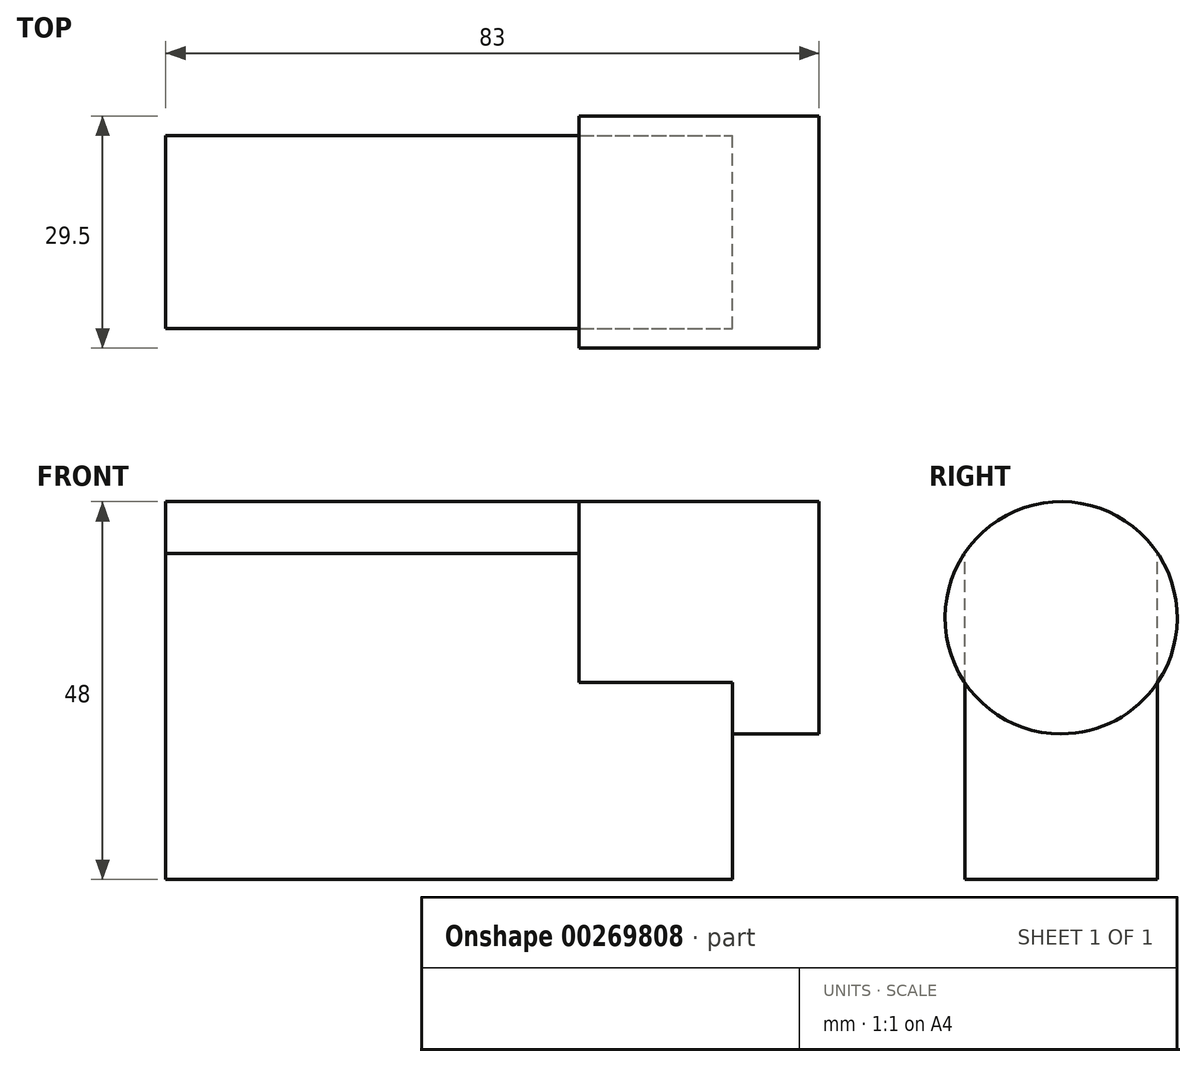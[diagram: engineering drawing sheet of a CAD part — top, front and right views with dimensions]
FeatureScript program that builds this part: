
annotation { "Feature Type Name" : "Feature", "Feature Type Description" : "" }
export const myFeature = defineFeature(function(context is Context, id is Id, definition is map)
    precondition{}
    {
        {
            var Q0;
            Q0=qCreatedBy(makeId("Top.planeOp"),FACE);
            var sketch = newSketch(context, id + "F0", { "sketchPlane" : qUnion([Q0])});
            skLineSegment(sketch, "E0.bottom", {"start": v(0, 0) * mm, "end": v(72, 0) * mm});
            skLineSegment(sketch, "E0.top", {"start": v(0, 24.5) * mm, "end": v(72, 24.5) * mm});
            skLineSegment(sketch, "E0.left", {"start": v(0, 0) * mm, "end": v(0, 24.5) * mm});
            skLineSegment(sketch, "E0.right", {"start": v(72, 0) * mm, "end": v(72, 24.5) * mm});
            skSolve(sketch);
        }
        {
            var Q0;
            Q0=makeQuery(id+"F0.imprint","IMPRINT",FACE,{"disambiguationData":[TD([[makeQuery(id+"F0.imprint","IMPRINT",EDGE,{"derivedFrom":sQuery(id+"F0.wireOp",EDGE,"E0.bottom")}),1.0]])]});
            extrude(context, id + "F1", {"entities" : qUnion([Q0]), "depth" : 18.5 * mm});
        }
        {
            var Q0;
            Q0=makeQuery(id+"F1.opExtrude","SWEPT_FACE",FACE,{"disambiguationData":[OSD([sQuery(id+"F0.wireOp",EDGE,"E0.right")])]});
            var sketch = newSketch(context, id + "F2", { "sketchPlane" : qUnion([Q0])});
            skCircle(sketch, "E1", {"center": v(12.25, 33.25) * mm, "radius": 14.75 * mm});
            skPoint(sketch, "E2", {"position": v(12.25, 18.5) * mm});
            skLineSegment(sketch, "E3", {"start": v(24.5, 18.5) * mm, "end": v(24.5, 41.44) * mm, "construction": true});
            skLineSegment(sketch, "E4", {"start": v(24.5, 41.44) * mm, "end": v(0, 41.44) * mm, "construction": true});
            skLineSegment(sketch, "E5", {"start": v(0, 41.44) * mm, "end": v(0, 18.5) * mm, "construction": true});
            skSolve(sketch);
        }
        {
            var Q0;
            Q0=makeQuery(id+"F2.imprint","IMPRINT",FACE,{"disambiguationData":[TD([[makeQuery(id+"F2.imprint","IMPRINT",EDGE,{"derivedFrom":sQuery(id+"F2.wireOp",EDGE,"E1")}),1.0]])]});
            extrude(context, id + "F3", {"entities" : qUnion([Q0]), "operationType" : NewBodyOperationType.ADD, "depth" : 11 * mm});
        }
        {
            var Q0;
            Q0=makeQuery(id+"F3.opExtrude","CAP_FACE",FACE,{"disambiguationData":[OSD([sQuery(id+"F2.wireOp",EDGE,"E1")])],"isStart":true});
            extrude(context, id + "F4", {"entities" : qUnion([Q0]), "depth" : 19.5 * mm});
        }
        {
            var Q0;
            Q0=makeQuery(id+"F1.opExtrude","CAP_FACE",FACE,{"disambiguationData":[OSD([sQuery(id+"F0.wireOp",EDGE,"E0.bottom"),sQuery(id+"F0.wireOp",EDGE,"E0.top"),sQuery(id+"F0.wireOp",EDGE,"E0.left"),sQuery(id+"F0.wireOp",EDGE,"E0.right")])],"isStart":false});
            var sketch = newSketch(context, id + "F5", { "sketchPlane" : qUnion([Q0])});
            skLineSegment(sketch, "E6.bottom", {"start": v(0, 0) * mm, "end": v(72, 0) * mm});
            skLineSegment(sketch, "E6.top", {"start": v(0, 24.5) * mm, "end": v(72, 24.5) * mm});
            skLineSegment(sketch, "E6.left", {"start": v(0, 0) * mm, "end": v(0, 24.5) * mm});
            skLineSegment(sketch, "E6.right", {"start": v(72, 0) * mm, "end": v(72, 24.5) * mm});
            skSolve(sketch);
        }
        {
            var Q0;
            Q0 = qSketchRegion(id + "F5", true);
            extrude(context, id + "F6", {"entities" : qUnion([Q0]), "operationType" : NewBodyOperationType.ADD, "depth" : 22.95 * mm});
        }
        {
            var Q0;
            Q0=makeQuery(id+"F6.opExtrude","SWEPT_FACE",FACE,{"disambiguationData":[OSD([sQuery(id+"F5.wireOp",EDGE,"E6.left")])]});
            var sketch = newSketch(context, id + "F7", { "sketchPlane" : qUnion([Q0])});
            skArc(sketch, "E7", {"start": v(0, 41.44) * mm, "mid": v(-12.25, 48) * mm, "end": v(-24.5, 41.44) * mm});
            skSolve(sketch);
        }
        {
            var Q0;
            Q0=makeQuery(id+"F7.imprint","IMPRINT",FACE,{"disambiguationData":[TD([[makeQuery(id+"F7.imprint","IMPRINT",EDGE,{"derivedFrom":sQuery(id+"F7.wireOp",EDGE,"E7")}),1.0]])]});
            extrude(context, id + "F8", {"entities" : qUnion([Q0]), "operationType" : NewBodyOperationType.ADD, "endBound" : BoundingType.UP_TO_NEXT, "oppositeDirection" : true, "depth" : 25 * mm});
        }
    });
